# Revit family: 1Electronics_Commercial-Audio_Biamp_Microphone-Discussion-System_MDS-Int
name_source: partatom
category: Communication Devices
units: mm (PartAtom-declared; Revit-internal decimal feet)

## family parameters
Cut with Voids When Loaded = No
Host = Face
Maintain Annotation Orientation = No
OmniClass Number = 23.85.10.11
Part Type = Normal
Room Calculation Point = No
Round Connector Dimension = Use Diameter
Shared = No

## types (1)
- INT
    Accessories supplied = power supply & cable, 1.5m 6.3 mm jack cable (unbalanced)
    Default Elevation = 4' - 0"
    Depth = 0' - 2"
    Description = MDS.INT Interface and PSU for Microphone Discussion System
    Height = 0' - 1"
    Housing Material = Biamp - Plastic - Black
    Manufacturer = Biamp
    Model = INT
    Nominal output level = 100 mV
    Output impedance = < 1 kohm
    Power supply in = 100 - 240 VAC/47-53Hz/1.4A max
    Power supply out = 15 VDC/4.3A switching mode power supply
    Product Documentation Link = https://downloads.biamp.com
    Product Page URL = https://www.biamp.com
    Product data url = https://www.bimobject.com
    Signal to noise ratio = > 60 dB
    System signal output = Unbalanced jack connector 6.3 mm
    THD = < 0.5%
    URL = https://www.biamp.com
    Weight = 1.32 lb
    Width = 0' - 2"

## geometry (parser evidence)
native form markers: Sweep x2
no freeform markers — native parametric forms only
